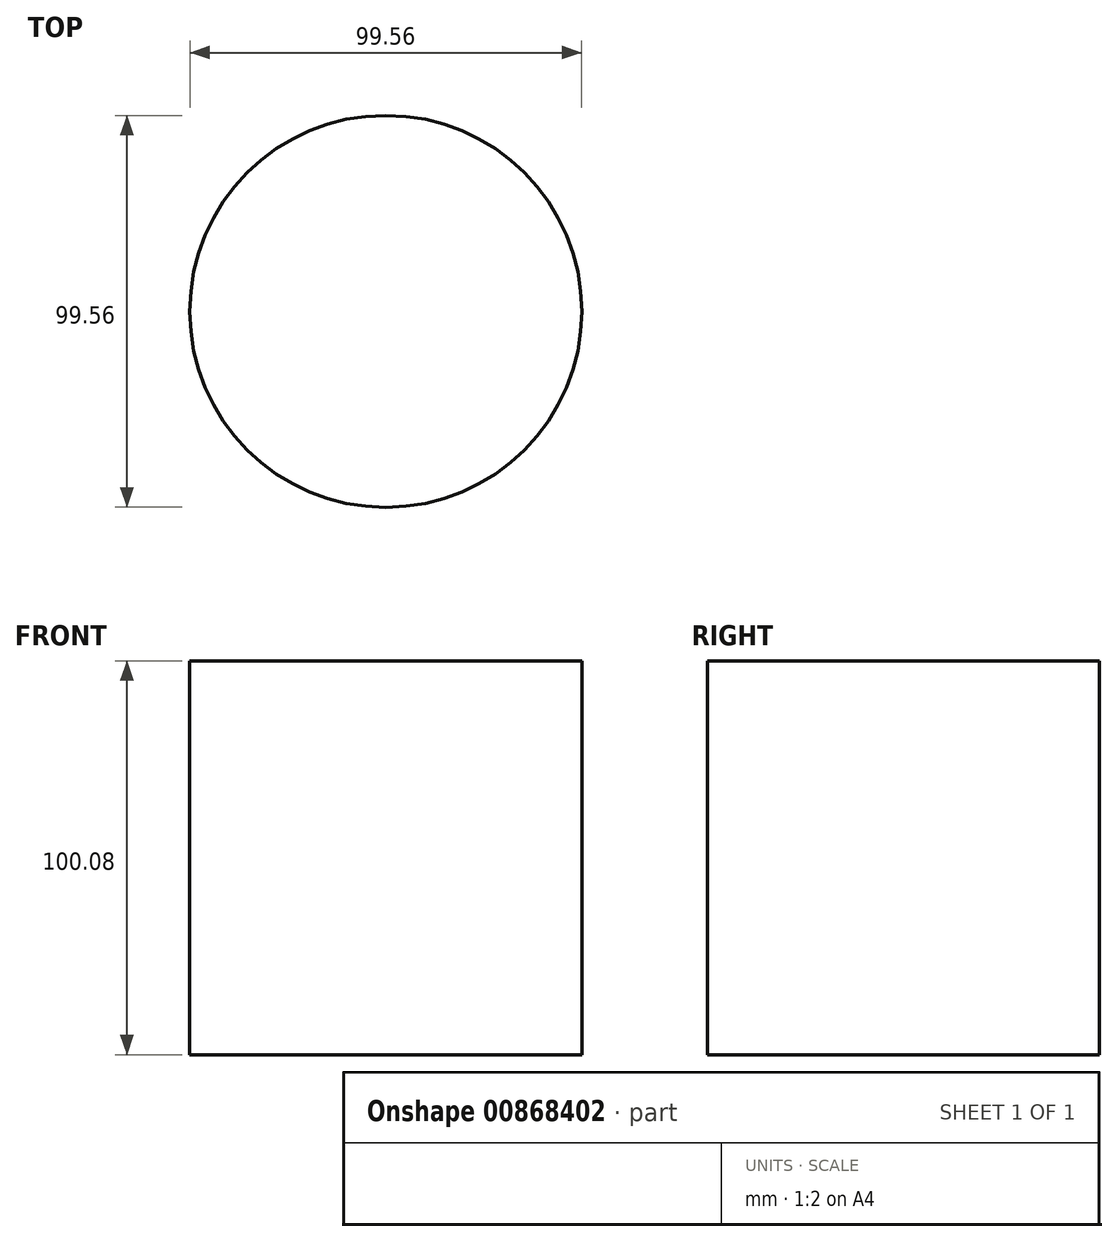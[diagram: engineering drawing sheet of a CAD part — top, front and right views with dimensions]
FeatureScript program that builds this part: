
annotation { "Feature Type Name" : "Feature", "Feature Type Description" : "" }
export const myFeature = defineFeature(function(context is Context, id is Id, definition is map)
    precondition{}
    {
        {
            var Q0;
            Q0=qCreatedBy(makeId("Top.planeOp"),FACE);
            var sketch = newSketch(context, id + "F0", { "sketchPlane" : qUnion([Q0])});
            skCircle(sketch, "E0", {"center": v(0, 0) * mm, "radius": 49.78 * mm});
            skSolve(sketch);
        }
        {
            var Q0;
            Q0=makeQuery(id+"F0.imprint","IMPRINT",FACE,{"disambiguationData":[TD([[makeQuery(id+"F0.imprint","IMPRINT",EDGE,{"derivedFrom":sQuery(id+"F0.wireOp",EDGE,"E0")}),1.0]])]});
            extrude(context, id + "F1", {"entities" : qUnion([Q0]), "depth" : 100.08 * mm, "offsetDistance" : 25.4 * mm});
        }
    });
